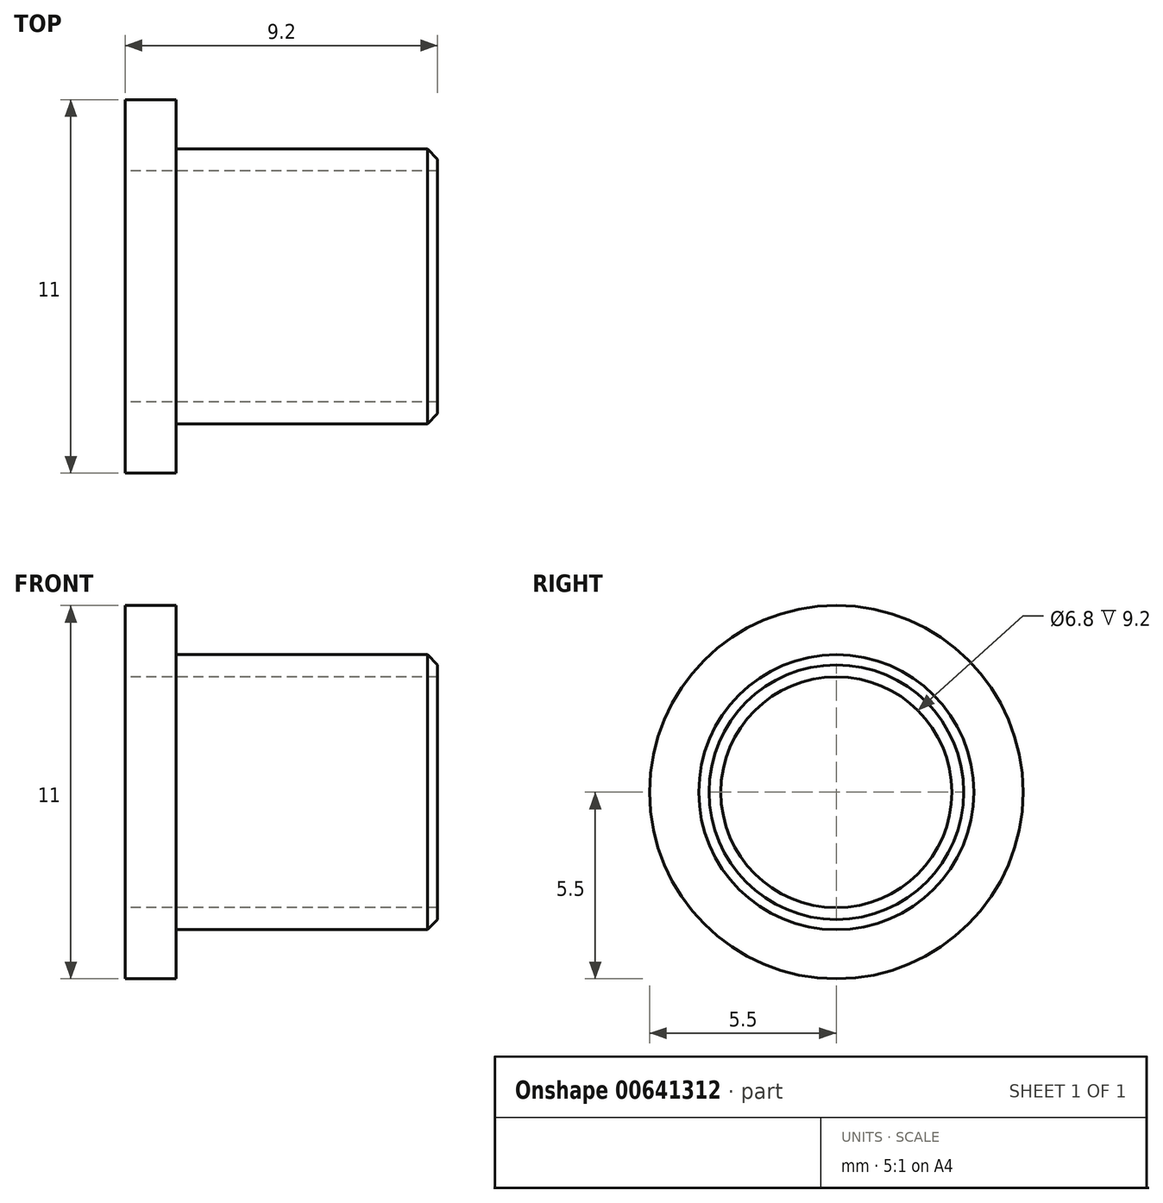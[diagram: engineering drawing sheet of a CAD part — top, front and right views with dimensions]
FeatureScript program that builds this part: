
annotation { "Feature Type Name" : "Feature", "Feature Type Description" : "" }
export const myFeature = defineFeature(function(context is Context, id is Id, definition is map)
    precondition{}
    {
        {
            var Q0;
            Q0=qCreatedBy(makeId("Right.planeOp"),FACE);
            var sketch = newSketch(context, id + "F0", { "sketchPlane" : qUnion([Q0])});
            skCircle(sketch, "E0", {"center": v(0, 0) * mm, "radius": 5.5 * mm});
            skCircle(sketch, "E1", {"center": v(0, 0) * mm, "radius": 4.05 * mm});
            skCircle(sketch, "E2", {"center": v(0, 0) * mm, "radius": 3.4 * mm});
            skSolve(sketch);
        }
        {
            var Q0;
            Q0=makeQuery(id+"F0.imprint","IMPRINT",FACE,{"disambiguationData":[TD([[makeQuery(id+"F0.imprint","IMPRINT",EDGE,{"derivedFrom":sQuery(id+"F0.wireOp",EDGE,"E1")}),1.0]])]});
            var Q1;
            Q1=makeQuery(id+"F0.imprint","IMPRINT",FACE,{"disambiguationData":[TD([[makeQuery(id+"F0.imprint","IMPRINT",EDGE,{"derivedFrom":sQuery(id+"F0.wireOp",EDGE,"E2")}),1.0]])]});
            var Q2;
            Q2=makeQuery(id+"F0.imprint","IMPRINT",FACE,{"disambiguationData":[TD([[makeQuery(id+"F0.imprint","IMPRINT",EDGE,{"derivedFrom":sQuery(id+"F0.wireOp",EDGE,"E0")}),1.0]])]});
            extrude(context, id + "F1", {"entities" : qUnion([Q0, Q1, Q2]), "depth" : 1.5 * mm, "offsetDistance" : 25 * mm});
        }
        {
            var Q0;
            Q0=makeQuery(id+"F0.imprint","IMPRINT",FACE,{"disambiguationData":[TD([[makeQuery(id+"F0.imprint","IMPRINT",EDGE,{"derivedFrom":sQuery(id+"F0.wireOp",EDGE,"E1")}),1.0]])]});
            extrude(context, id + "F2", {"entities" : qUnion([Q0]), "operationType" : NewBodyOperationType.ADD, "depth" : (1.5 + 7.7) * mm, "offsetDistance" : 25 * mm});
        }
        {
            var Q0;
            Q0=makeQuery(id+"F0.imprint","IMPRINT",FACE,{"disambiguationData":[TD([[makeQuery(id+"F0.imprint","IMPRINT",EDGE,{"derivedFrom":sQuery(id+"F0.wireOp",EDGE,"E2")}),1.0]])]});
            extrude(context, id + "F3", {"entities" : qUnion([Q0]), "operationType" : NewBodyOperationType.REMOVE, "endBound" : BoundingType.THROUGH_ALL, "depth" : 25 * mm, "offsetDistance" : 25 * mm});
        }
        {
            var Q0;
            Q0=makeQuery(id+"F3.boolean.opBoolean","COPY",EDGE,{"derivedFrom":makeQuery(id+"F3.opExtrude","CAP_EDGE",EDGE,{"disambiguationData":[OSD([sQuery(id+"F0.wireOp",EDGE,"E2")])],"isStart":true})});
            var Q1;
            Q1=makeQuery(id+"F2.opExtrude","CAP_EDGE",EDGE,{"disambiguationData":[OSD([sQuery(id+"F0.wireOp",EDGE,"E1")])],"isStart":false});
            chamfer(context, id + "F4", {"entities" : qUnion([Q0, Q1]), "width" : 0.3 * mm, "tangentPropagation" : true});
        }
    });
